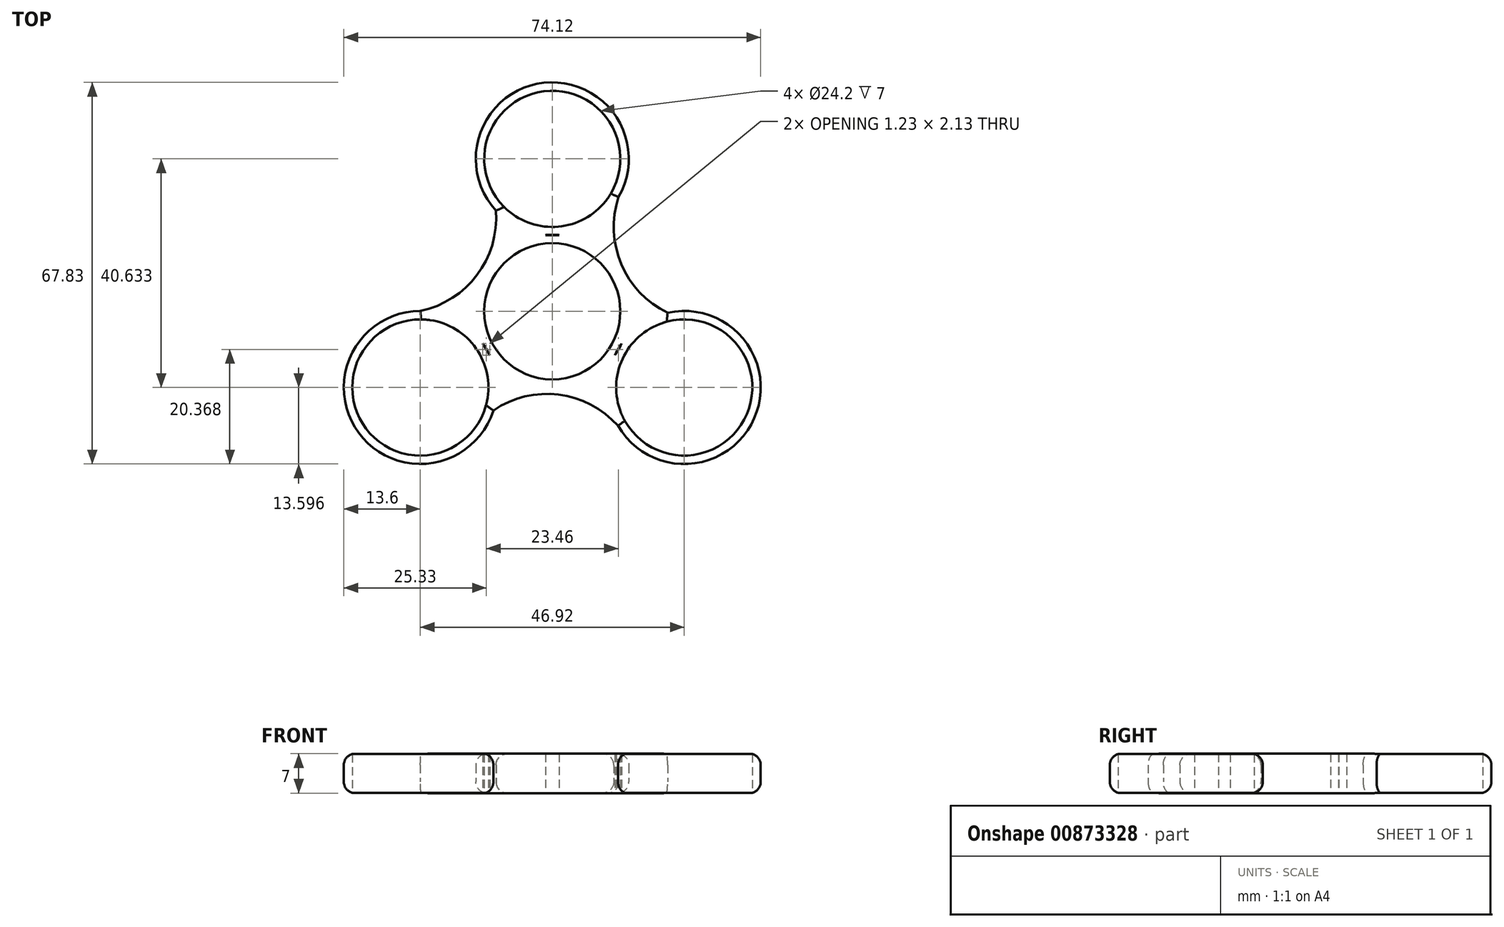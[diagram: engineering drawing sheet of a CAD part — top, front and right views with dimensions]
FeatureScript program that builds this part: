
annotation { "Feature Type Name" : "Feature", "Feature Type Description" : "" }
export const myFeature = defineFeature(function(context is Context, id is Id, definition is map)
    precondition{}
    {
        {
            var Q0;
            Q0=qCreatedBy(makeId("Top.planeOp"),FACE);
            var sketch = newSketch(context, id + "F0", { "sketchPlane" : qUnion([Q0])});
            skCircle(sketch, "E0", {"center": v(0, 0) * mm, "radius": 12.1 * mm});
            skCircle(sketch, "E1", {"center": v(0, 0) * mm, "radius": 13.6 * mm});
            skCircle(sketch, "E2", {"center": v(0, 27.09) * mm, "radius": 12.1 * mm});
            skCircle(sketch, "E3", {"center": v(0, 27.09) * mm, "radius": 13.6 * mm});
            skCircle(sketch, "E4.1.0", {"center": v(-23.46, -13.54) * mm, "radius": 13.6 * mm});
            skCircle(sketch, "E4.1.1", {"center": v(-23.46, -13.54) * mm, "radius": 12.1 * mm});
            skCircle(sketch, "E4.2.0", {"center": v(23.46, -13.54) * mm, "radius": 13.6 * mm});
            skCircle(sketch, "E4.2.1", {"center": v(23.46, -13.54) * mm, "radius": 12.1 * mm});
            skArc(sketch, "E5", {"start": v(-23.46, 0.06) * mm, "mid": v(-11, 10.82) * mm, "end": v(-13.6, 27.09) * mm});
            skArc(sketch, "E6.1.0", {"start": v(11.68, -20.34) * mm, "mid": v(-3.88, -14.94) * mm, "end": v(-16.66, -25.32) * mm});
            skArc(sketch, "E6.2.0", {"start": v(11.78, 20.29) * mm, "mid": v(14.87, 4.11) * mm, "end": v(30.26, -1.77) * mm});
            skSolve(sketch);
        }
        {
            var Q0;
            {var subQ0=sQuery(id+"F0.wireOp",EDGE,"E4.1.0");var subQ2=sQuery(id+"F0.wireOp",EDGE,"E1");var subQ3=makeQuery(id+"F0.imprint","INTERSECT",VERTEX,{"disambiguationData":[OD(0.0)],"derivedFrom":[subQ2,subQ0]});Q0=makeQuery(id+"F0.imprint","IMPRINT",FACE,{"disambiguationData":[TD([[makeQuery(id+"F0.imprint","IMPRINT",EDGE,{"disambiguationData":[TD([[subQ3,-1.0]])],"derivedFrom":subQ2}),-1.0]])]});}
            var Q1;
            {var subQ0=sQuery(id+"F0.wireOp",EDGE,"E6.1.0");var subQ1=sQuery(id+"F0.wireOp",EDGE,"E4.1.0");var subQ2=makeQuery(id+"F0.imprint","INTERSECT",VERTEX,{"disambiguationData":[OD(0.0)],"derivedFrom":[subQ1,subQ0]});Q1=makeQuery(id+"F0.imprint","IMPRINT",FACE,{"disambiguationData":[TD([[makeQuery(id+"F0.imprint","IMPRINT",EDGE,{"disambiguationData":[TD([[subQ2,-1.0]])],"derivedFrom":subQ1}),1.0]])]});}
            var Q2;
            {var subQ0=sQuery(id+"F0.wireOp",EDGE,"E4.1.0");var subQ1=sQuery(id+"F0.wireOp",EDGE,"E1");var subQ2=makeQuery(id+"F0.imprint","INTERSECT",VERTEX,{"disambiguationData":[OD(1.0)],"derivedFrom":[subQ1,subQ0]});Q2=makeQuery(id+"F0.imprint","IMPRINT",FACE,{"disambiguationData":[TD([[makeQuery(id+"F0.imprint","IMPRINT",EDGE,{"disambiguationData":[TD([[subQ2,-1.0]])],"derivedFrom":subQ1}),-1.0]])]});}
            var Q3;
            {var subQ0=sQuery(id+"F0.wireOp",EDGE,"E3");var subQ1=sQuery(id+"F0.wireOp",EDGE,"E1");var subQ2=makeQuery(id+"F0.imprint","INTERSECT",VERTEX,{"disambiguationData":[OD(1.0)],"derivedFrom":[subQ1,subQ0]});Q3=makeQuery(id+"F0.imprint","IMPRINT",FACE,{"disambiguationData":[TD([[makeQuery(id+"F0.imprint","IMPRINT",EDGE,{"disambiguationData":[TD([[subQ2,1.0]])],"derivedFrom":subQ1}),-1.0]])]});}
            var Q4;
            {var subQ0=sQuery(id+"F0.wireOp",EDGE,"E3");var subQ1=sQuery(id+"F0.wireOp",EDGE,"E1");var subQ2=makeQuery(id+"F0.imprint","INTERSECT",VERTEX,{"disambiguationData":[OD(0.0)],"derivedFrom":[subQ1,subQ0]});Q4=makeQuery(id+"F0.imprint","IMPRINT",FACE,{"disambiguationData":[TD([[makeQuery(id+"F0.imprint","IMPRINT",EDGE,{"disambiguationData":[TD([[subQ2,-1.0]])],"derivedFrom":subQ1}),-1.0]])]});}
            var Q5;
            Q5=makeQuery(id+"F0.imprint","IMPRINT",FACE,{"disambiguationData":[TD([[makeQuery(id+"F0.imprint","IMPRINT",EDGE,{"derivedFrom":sQuery(id+"F0.wireOp",EDGE,"E0")}),-1.0]])]});
            var Q6;
            {var subQ0=sQuery(id+"F0.wireOp",EDGE,"E3");var subQ2=sQuery(id+"F0.wireOp",EDGE,"E1");var subQ4=makeQuery(id+"F0.imprint","INTERSECT",VERTEX,{"disambiguationData":[OD(0.0)],"derivedFrom":[subQ2,subQ0]});Q6=makeQuery(id+"F0.imprint","IMPRINT",FACE,{"disambiguationData":[TD([[makeQuery(id+"F0.imprint","IMPRINT",EDGE,{"disambiguationData":[TD([[subQ4,1.0]])],"derivedFrom":subQ2}),-1.0]])]});}
            var Q7;
            {var subQ0=sQuery(id+"F0.wireOp",EDGE,"E5");var subQ1=sQuery(id+"F0.wireOp",EDGE,"E2");var subQ2=makeQuery(id+"F0.imprint","INTERSECT",VERTEX,{"disambiguationData":[OD(0.0)],"derivedFrom":[subQ1,subQ0]});Q7=makeQuery(id+"F0.imprint","IMPRINT",FACE,{"disambiguationData":[TD([[makeQuery(id+"F0.imprint","IMPRINT",EDGE,{"disambiguationData":[TD([[subQ2,1.0]])],"derivedFrom":subQ1}),-1.0]])]});}
            var Q8;
            {var subQ0=sQuery(id+"F0.wireOp",EDGE,"E6.2.0");var subQ1=sQuery(id+"F0.wireOp",EDGE,"E4.2.0");var subQ2=makeQuery(id+"F0.imprint","INTERSECT",VERTEX,{"disambiguationData":[OD(0.0)],"derivedFrom":[subQ1,subQ0]});Q8=makeQuery(id+"F0.imprint","IMPRINT",FACE,{"disambiguationData":[TD([[makeQuery(id+"F0.imprint","IMPRINT",EDGE,{"disambiguationData":[TD([[subQ2,-1.0]])],"derivedFrom":subQ1}),1.0]])]});}
            var Q9;
            {var subQ0=sQuery(id+"F0.wireOp",EDGE,"E4.2.0");var subQ2=sQuery(id+"F0.wireOp",EDGE,"E1");var subQ3=makeQuery(id+"F0.imprint","INTERSECT",VERTEX,{"disambiguationData":[OD(0.0)],"derivedFrom":[subQ2,subQ0]});Q9=makeQuery(id+"F0.imprint","IMPRINT",FACE,{"disambiguationData":[TD([[makeQuery(id+"F0.imprint","IMPRINT",EDGE,{"disambiguationData":[TD([[subQ3,-1.0]])],"derivedFrom":subQ2}),-1.0]])]});}
            extrude(context, id + "F1", {"entities" : qUnion([Q0, Q1, Q2, Q3, Q4, Q5, Q6, Q7, Q8, Q9]), "depth" : 7 * mm, "offsetDistance" : 25 * mm});
        }
        {
            var Q0;
            Q0=makeQuery(id+"F1.opExtrude","CAP_EDGE",EDGE,{"disambiguationData":[OSD([sQuery(id+"F0.wireOp",EDGE,"E6.1.0")])],"isStart":false});
            var Q1;
            {var subQ0=sQuery(id+"F0.wireOp",EDGE,"E4.1.0");var subQ1=sQuery(id+"F0.wireOp",EDGE,"E6.1.0");var subQ2=makeQuery(id+"F0.imprint","INTERSECT",VERTEX,{"disambiguationData":[OD(0.0)],"derivedFrom":[subQ0,subQ1]});Q1=makeQuery(id+"F1.opExtrude","CAP_EDGE",EDGE,{"disambiguationData":[OSD([subQ0]),TDD([makeQuery(id+"F0.imprint","IMPRINT",EDGE,{"disambiguationData":[TD([[subQ2,-1.0]])],"derivedFrom":subQ0}),makeQuery(id+"F0.imprint","IMPRINT",EDGE,{"disambiguationData":[TD([[makeQuery(id+"F0.imprint","INTERSECT",VERTEX,{"derivedFrom":[subQ0,sQuery(id+"F0.wireOp",EDGE,"E5")]}),-1.0]])],"derivedFrom":subQ0})])],"isStart":false});}
            var Q2;
            Q2=makeQuery(id+"F1.opExtrude","CAP_EDGE",EDGE,{"disambiguationData":[OSD([sQuery(id+"F0.wireOp",EDGE,"E5")])],"isStart":false});
            var Q3;
            {var subQ0=sQuery(id+"F0.wireOp",EDGE,"E5");var subQ1=sQuery(id+"F0.wireOp",EDGE,"E3");var subQ2=makeQuery(id+"F0.imprint","INTERSECT",VERTEX,{"disambiguationData":[OD(0.0)],"derivedFrom":[subQ1,subQ0]});Q3=makeQuery(id+"F1.opExtrude","CAP_EDGE",EDGE,{"disambiguationData":[OSD([subQ1]),TDD([makeQuery(id+"F0.imprint","IMPRINT",EDGE,{"disambiguationData":[TD([[subQ2,-1.0]])],"derivedFrom":subQ1}),makeQuery(id+"F0.imprint","IMPRINT",EDGE,{"disambiguationData":[TD([[subQ2,1.0]])],"derivedFrom":subQ1})])],"isStart":false});}
            var Q4;
            Q4=makeQuery(id+"F1.opExtrude","CAP_EDGE",EDGE,{"disambiguationData":[OSD([sQuery(id+"F0.wireOp",EDGE,"E6.2.0")])],"isStart":false});
            var Q5;
            {var subQ0=sQuery(id+"F0.wireOp",EDGE,"E4.2.0");var subQ1=sQuery(id+"F0.wireOp",EDGE,"E6.2.0");var subQ2=makeQuery(id+"F0.imprint","INTERSECT",VERTEX,{"disambiguationData":[OD(0.0)],"derivedFrom":[subQ0,subQ1]});Q5=makeQuery(id+"F1.opExtrude","CAP_EDGE",EDGE,{"disambiguationData":[OSD([subQ0]),TDD([makeQuery(id+"F0.imprint","IMPRINT",EDGE,{"disambiguationData":[TD([[subQ2,-1.0]])],"derivedFrom":subQ0}),makeQuery(id+"F0.imprint","IMPRINT",EDGE,{"disambiguationData":[TD([[makeQuery(id+"F0.imprint","INTERSECT",VERTEX,{"derivedFrom":[subQ0,sQuery(id+"F0.wireOp",EDGE,"E6.1.0")]}),-1.0]])],"derivedFrom":subQ0})])],"isStart":false});}
            var Q6;
            Q6=makeQuery(id+"F1.opExtrude","CAP_EDGE",EDGE,{"disambiguationData":[OSD([sQuery(id+"F0.wireOp",EDGE,"E6.1.0")])],"isStart":true});
            var Q7;
            Q7=makeQuery(id+"F1.opExtrude","CAP_EDGE",EDGE,{"disambiguationData":[OSD([sQuery(id+"F0.wireOp",EDGE,"E6.2.0")])],"isStart":true});
            var Q8;
            {var subQ0=sQuery(id+"F0.wireOp",EDGE,"E4.2.0");var subQ1=sQuery(id+"F0.wireOp",EDGE,"E6.2.0");var subQ2=makeQuery(id+"F0.imprint","INTERSECT",VERTEX,{"disambiguationData":[OD(0.0)],"derivedFrom":[subQ0,subQ1]});Q8=makeQuery(id+"F1.opExtrude","CAP_EDGE",EDGE,{"disambiguationData":[OSD([subQ0]),TDD([makeQuery(id+"F0.imprint","IMPRINT",EDGE,{"disambiguationData":[TD([[subQ2,-1.0]])],"derivedFrom":subQ0}),makeQuery(id+"F0.imprint","IMPRINT",EDGE,{"disambiguationData":[TD([[makeQuery(id+"F0.imprint","INTERSECT",VERTEX,{"derivedFrom":[subQ0,sQuery(id+"F0.wireOp",EDGE,"E6.1.0")]}),-1.0]])],"derivedFrom":subQ0})])],"isStart":true});}
            var Q9;
            {var subQ0=sQuery(id+"F0.wireOp",EDGE,"E4.1.0");var subQ1=sQuery(id+"F0.wireOp",EDGE,"E6.1.0");var subQ2=makeQuery(id+"F0.imprint","INTERSECT",VERTEX,{"disambiguationData":[OD(0.0)],"derivedFrom":[subQ0,subQ1]});Q9=makeQuery(id+"F1.opExtrude","CAP_EDGE",EDGE,{"disambiguationData":[OSD([subQ0]),TDD([makeQuery(id+"F0.imprint","IMPRINT",EDGE,{"disambiguationData":[TD([[subQ2,-1.0]])],"derivedFrom":subQ0}),makeQuery(id+"F0.imprint","IMPRINT",EDGE,{"disambiguationData":[TD([[makeQuery(id+"F0.imprint","INTERSECT",VERTEX,{"derivedFrom":[subQ0,sQuery(id+"F0.wireOp",EDGE,"E5")]}),-1.0]])],"derivedFrom":subQ0})])],"isStart":true});}
            var Q10;
            {var subQ0=sQuery(id+"F0.wireOp",EDGE,"E5");var subQ1=sQuery(id+"F0.wireOp",EDGE,"E3");var subQ2=makeQuery(id+"F0.imprint","INTERSECT",VERTEX,{"disambiguationData":[OD(0.0)],"derivedFrom":[subQ1,subQ0]});Q10=makeQuery(id+"F1.opExtrude","CAP_EDGE",EDGE,{"disambiguationData":[OSD([subQ1]),TDD([makeQuery(id+"F0.imprint","IMPRINT",EDGE,{"disambiguationData":[TD([[subQ2,-1.0]])],"derivedFrom":subQ1}),makeQuery(id+"F0.imprint","IMPRINT",EDGE,{"disambiguationData":[TD([[subQ2,1.0]])],"derivedFrom":subQ1})])],"isStart":true});}
            var Q11;
            Q11=makeQuery(id+"F1.opExtrude","CAP_EDGE",EDGE,{"disambiguationData":[OSD([sQuery(id+"F0.wireOp",EDGE,"E5")])],"isStart":true});
            fillet(context, id + "F2", {"entities" : qUnion([Q0, Q1, Q2, Q3, Q4, Q5, Q6, Q7, Q8, Q9, Q10, Q11]), "radius" : 2 * mm, "tangentPropagation" : true, "allowEdgeOverflow" : false});
        }
    });
